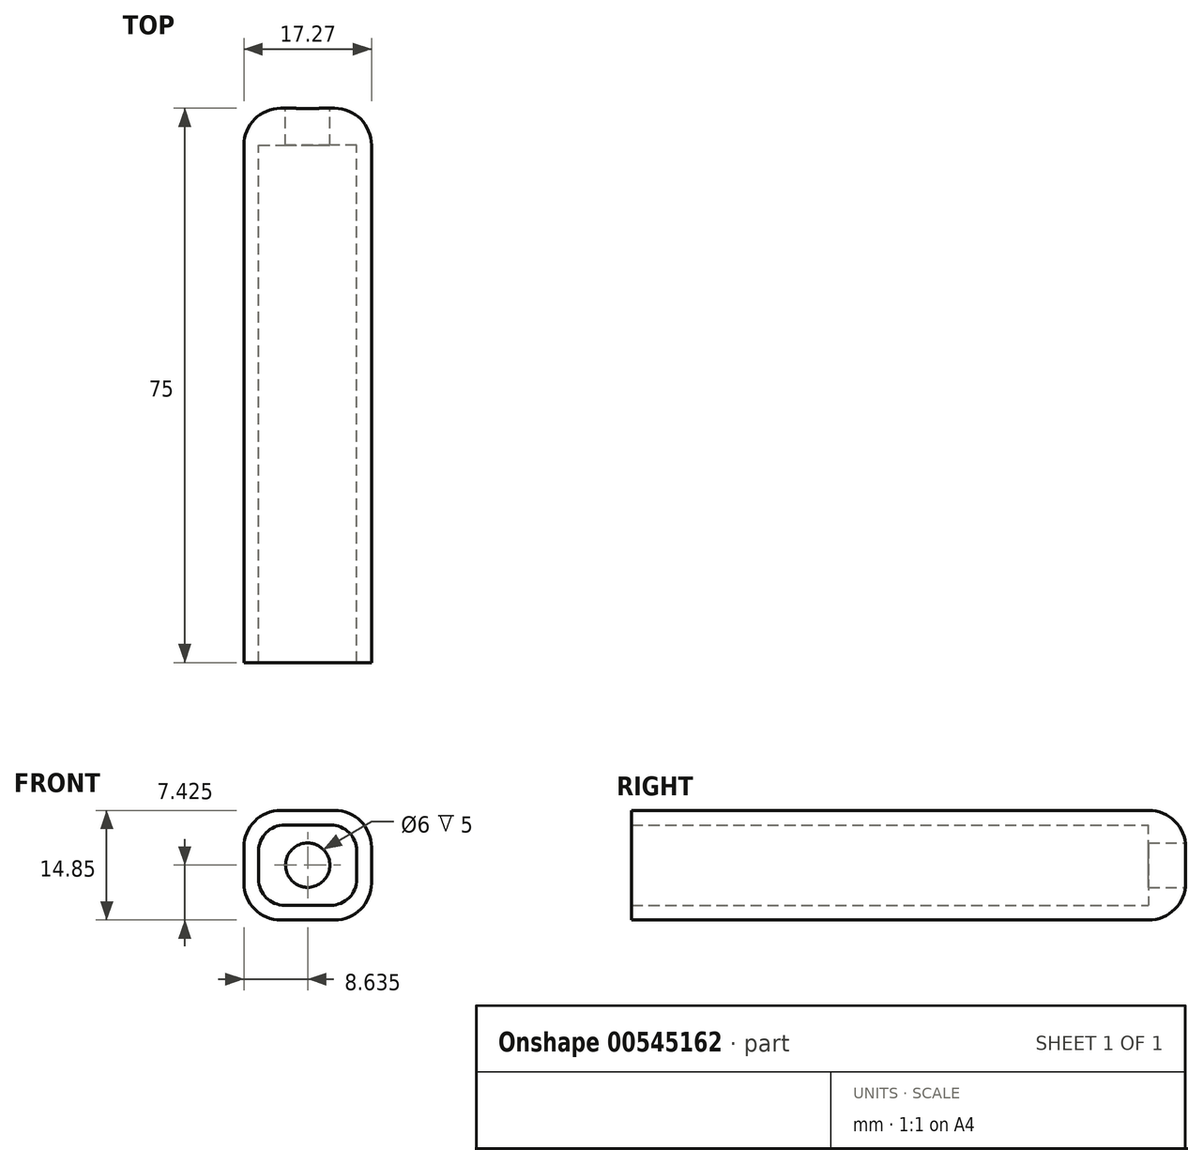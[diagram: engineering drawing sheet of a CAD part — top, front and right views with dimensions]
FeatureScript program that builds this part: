
annotation { "Feature Type Name" : "Feature", "Feature Type Description" : "" }
export const myFeature = defineFeature(function(context is Context, id is Id, definition is map)
    precondition{}
    {
        {
            var Q0;
            Q0=qCreatedBy(makeId("Front.planeOp"),FACE);
            var sketch = newSketch(context, id + "F0", { "sketchPlane" : qUnion([Q0])});
            skLineSegment(sketch, "E0.bottom", {"start": v(0, 0) * mm, "end": v(13.27, 0) * mm});
            skLineSegment(sketch, "E0.top", {"start": v(0, 10.85) * mm, "end": v(13.27, 10.85) * mm});
            skLineSegment(sketch, "E0.left", {"start": v(0, 0) * mm, "end": v(0, 10.85) * mm});
            skLineSegment(sketch, "E0.right", {"start": v(13.27, 0) * mm, "end": v(13.27, 10.85) * mm});
            skLineSegment(sketch, "E1.bottom", {"start": v(-2, -2) * mm, "end": v(15.27, -2) * mm});
            skLineSegment(sketch, "E1.top", {"start": v(-2, 12.85) * mm, "end": v(15.27, 12.85) * mm});
            skLineSegment(sketch, "E1.left", {"start": v(-2, -2) * mm, "end": v(-2, 12.85) * mm});
            skLineSegment(sketch, "E1.right", {"start": v(15.27, -2) * mm, "end": v(15.27, 12.85) * mm});
            skSolve(sketch);
        }
        {
            var Q0;
            Q0=makeQuery(id+"F0.imprint","IMPRINT",FACE,{"disambiguationData":[TD([[makeQuery(id+"F0.imprint","IMPRINT",EDGE,{"derivedFrom":sQuery(id+"F0.wireOp",EDGE,"E0.bottom")}),-1.0]])]});
            extrude(context, id + "F1", {"entities" : qUnion([Q0]), "depth" : 75 * mm, "offsetDistance" : 25 * mm});
        }
        {
            var Q0;
            Q0=makeQuery(id+"F1.opExtrude","SWEPT_EDGE",EDGE,{"disambiguationData":[OSD([sQuery(id+"F0.wireOp",EDGE,"E0.top"),sQuery(id+"F0.wireOp",EDGE,"E0.left")])]});
            var Q1;
            Q1=makeQuery(id+"F1.opExtrude","SWEPT_EDGE",EDGE,{"disambiguationData":[OSD([sQuery(id+"F0.wireOp",EDGE,"E0.bottom"),sQuery(id+"F0.wireOp",EDGE,"E0.right")])]});
            var Q2;
            Q2=makeQuery(id+"F1.opExtrude","SWEPT_EDGE",EDGE,{"disambiguationData":[OSD([sQuery(id+"F0.wireOp",EDGE,"E0.top"),sQuery(id+"F0.wireOp",EDGE,"E0.right")])]});
            var Q3;
            Q3=makeQuery(id+"F1.opExtrude","SWEPT_EDGE",EDGE,{"disambiguationData":[OSD([sQuery(id+"F0.wireOp",EDGE,"E0.bottom"),sQuery(id+"F0.wireOp",EDGE,"E0.left")])]});
            fillet(context, id + "F2", {"entities" : qUnion([Q0, Q1, Q2, Q3]), "radius" : 3.5 * mm, "tangentPropagation" : true, "allowEdgeOverflow" : false});
        }
        {
            var Q0;
            Q0=makeQuery(id+"F1.opExtrude","SWEPT_EDGE",EDGE,{"disambiguationData":[OSD([sQuery(id+"F0.wireOp",EDGE,"E1.top"),sQuery(id+"F0.wireOp",EDGE,"E1.left")])]});
            var Q1;
            Q1=makeQuery(id+"F1.opExtrude","SWEPT_EDGE",EDGE,{"disambiguationData":[OSD([sQuery(id+"F0.wireOp",EDGE,"E1.top"),sQuery(id+"F0.wireOp",EDGE,"E1.right")])]});
            var Q2;
            Q2=makeQuery(id+"F1.opExtrude","SWEPT_EDGE",EDGE,{"disambiguationData":[OSD([sQuery(id+"F0.wireOp",EDGE,"E1.bottom"),sQuery(id+"F0.wireOp",EDGE,"E1.right")])]});
            var Q3;
            Q3=makeQuery(id+"F1.opExtrude","SWEPT_EDGE",EDGE,{"disambiguationData":[OSD([sQuery(id+"F0.wireOp",EDGE,"E1.bottom"),sQuery(id+"F0.wireOp",EDGE,"E1.left")])]});
            fillet(context, id + "F3", {"entities" : qUnion([Q0, Q1, Q2, Q3]), "radius" : 5 * mm, "tangentPropagation" : true, "allowEdgeOverflow" : false});
        }
        {
            var Q0;
            Q0=makeQuery(id+"F0.imprint","IMPRINT",FACE,{"disambiguationData":[TD([[makeQuery(id+"F0.imprint","IMPRINT",EDGE,{"derivedFrom":sQuery(id+"F0.wireOp",EDGE,"E0.bottom")}),-1.0]])]});
            var sketch = newSketch(context, id + "F4", { "sketchPlane" : qUnion([Q0])});
            skLineSegment(sketch, "E2.bottom", {"start": v(13.27, 10.85) * mm, "end": v(0, 10.85) * mm});
            skLineSegment(sketch, "E2.top", {"start": v(13.27, 0) * mm, "end": v(0, 0) * mm});
            skLineSegment(sketch, "E2.left", {"start": v(13.27, 10.85) * mm, "end": v(13.27, 0) * mm});
            skLineSegment(sketch, "E2.right", {"start": v(0, 10.85) * mm, "end": v(0, 0) * mm});
            skSolve(sketch);
        }
        {
            var Q0;
            Q0 = qSketchRegion(id + "F4", true);
            extrude(context, id + "F5", {"entities" : qUnion([Q0]), "operationType" : NewBodyOperationType.ADD, "depth" : 5 * mm, "offsetDistance" : 25 * mm});
        }
        {
            var Q0;
            Q0=makeQuery(id+"F0.imprint","IMPRINT",FACE,{"disambiguationData":[TD([[makeQuery(id+"F0.imprint","IMPRINT",EDGE,{"derivedFrom":sQuery(id+"F0.wireOp",EDGE,"E0.bottom")}),1.0]])]});
            var sketch = newSketch(context, id + "F6", { "sketchPlane" : qUnion([Q0])});
            skCircle(sketch, "E3", {"center": v(6.63, 5.42) * mm, "radius": 3 * mm});
            skSolve(sketch);
        }
        {
            var Q0;
            Q0=makeQuery(id+"F6.imprint","IMPRINT",FACE,{"disambiguationData":[TD([[makeQuery(id+"F6.imprint","IMPRINT",EDGE,{"derivedFrom":sQuery(id+"F6.wireOp",EDGE,"E3")}),1.0]])]});
            extrude(context, id + "F7", {"entities" : qUnion([Q0]), "operationType" : NewBodyOperationType.REMOVE, "depth" : 25 * mm, "offsetDistance" : 25 * mm});
        }
        {
            var Q0;
            Q0=makeQuery(id+"F1.opExtrude","CAP_EDGE",EDGE,{"disambiguationData":[OSD([sQuery(id+"F0.wireOp",EDGE,"E1.top")])],"isStart":true});
            fillet(context, id + "F8", {"entities" : qUnion([Q0]), "radius" : 5 * mm, "tangentPropagation" : true, "allowEdgeOverflow" : false});
        }
    });
